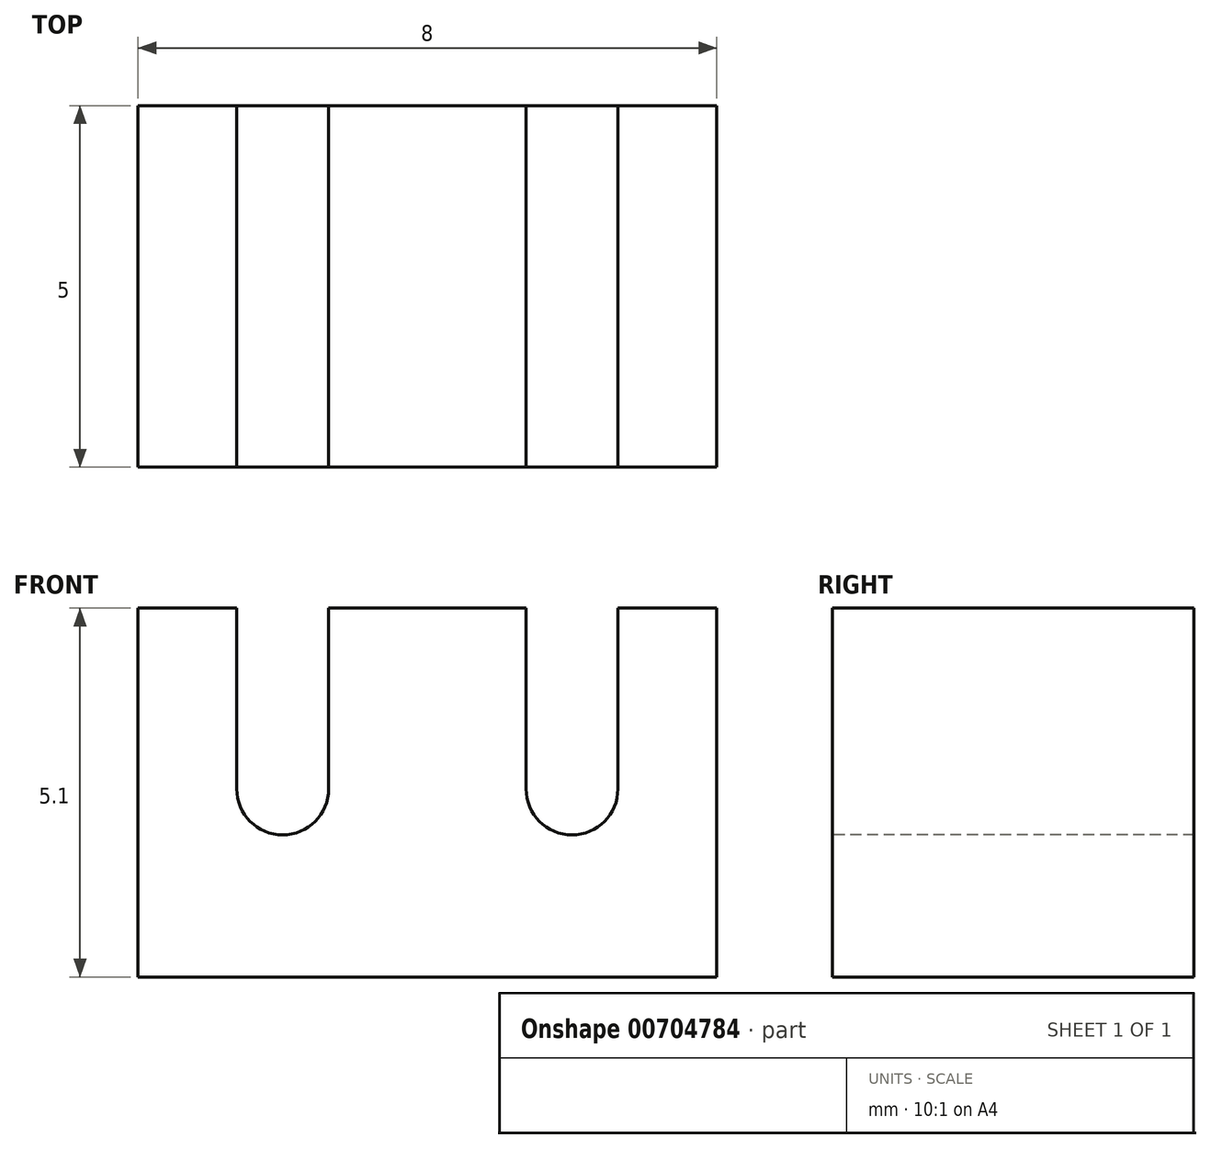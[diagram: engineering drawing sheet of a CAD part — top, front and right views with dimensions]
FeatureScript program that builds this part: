
annotation { "Feature Type Name" : "Feature", "Feature Type Description" : "" }
export const myFeature = defineFeature(function(context is Context, id is Id, definition is map)
    precondition{}
    {
        {
            var Q0;
            Q0=qCreatedBy(makeId("Top.planeOp"),FACE);
            var sketch = newSketch(context, id + "F0", { "sketchPlane" : qUnion([Q0])});
            skLineSegment(sketch, "E0.bottom", {"start": v(4, 2.5) * mm, "end": v(-4, 2.5) * mm});
            skLineSegment(sketch, "E0.top", {"start": v(4, -2.5) * mm, "end": v(-4, -2.5) * mm});
            skLineSegment(sketch, "E0.left", {"start": v(4, 2.5) * mm, "end": v(4, -2.5) * mm});
            skLineSegment(sketch, "E0.right", {"start": v(-4, 2.5) * mm, "end": v(-4, -2.5) * mm});
            skPoint(sketch, "E0.middle", {"position": v(0, 0) * mm});
            skSolve(sketch);
        }
        {
            var Q0;
            Q0 = qSketchRegion(id + "F0", true);
            extrude(context, id + "F1", {"entities" : qUnion([Q0]), "depth" : 5.1 * mm, "offsetDistance" : 25 * mm});
        }
        {
            var Q0;
            Q0=makeQuery(id+"F1.opExtrude","SWEPT_FACE",FACE,{"disambiguationData":[OSD([sQuery(id+"F0.wireOp",EDGE,"E0.top")])]});
            var sketch = newSketch(context, id + "F2", { "sketchPlane" : qUnion([Q0])});
            skLineSegment(sketch, "E1", {"start": v(0, 5.1) * mm, "end": v(2, 5.1) * mm});
            skLineSegment(sketch, "E2", {"start": v(2, 5.1) * mm, "end": v(2, 2.6) * mm});
            skCircle(sketch, "E3", {"center": v(2, 2.6) * mm, "radius": 0.63 * mm});
            skLineSegment(sketch, "E4", {"start": v(1.37, 2.6) * mm, "end": v(1.37, 5.1) * mm});
            skLineSegment(sketch, "E5", {"start": v(2.63, 2.6) * mm, "end": v(2.63, 5.1) * mm});
            skLineSegment(sketch, "E6", {"start": v(2.63, 5.1) * mm, "end": v(2, 5.1) * mm});
            skLineSegment(sketch, "E7", {"start": v(0, 5.1) * mm, "end": v(0, 4.51) * mm});
            skLineSegment(sketch, "E8.MirrorCS", {"start": v(-1.37, 2.6) * mm, "end": v(-1.37, 5.1) * mm});
            skCircle(sketch, "E9.MirrorC", {"center": v(-2, 2.6) * mm, "radius": 0.63 * mm});
            skLineSegment(sketch, "E10.MirrorCS", {"start": v(-2.63, 2.6) * mm, "end": v(-2.63, 5.1) * mm});
            skLineSegment(sketch, "E11.MirrorCS", {"start": v(-2.63, 5.1) * mm, "end": v(-2, 5.1) * mm});
            skLineSegment(sketch, "E12.MirrorCS", {"start": v(0, 5.1) * mm, "end": v(-2, 5.1) * mm});
            skSolve(sketch);
        }
        {
            var Q0;
            Q0 = qSketchRegion(id + "F2", true);
            extrude(context, id + "F3", {"entities" : qUnion([Q0]), "operationType" : NewBodyOperationType.REMOVE, "oppositeDirection" : true, "depth" : 25 * mm, "offsetDistance" : 25 * mm});
        }
    });
